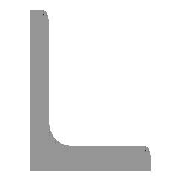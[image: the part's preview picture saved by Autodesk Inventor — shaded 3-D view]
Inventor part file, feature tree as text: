
AUTODESK INVENTOR PART (.ipt)
format: ipt  version: 2013 (Build 170138000, 138)  size: 116,736 bytes
history: native  units: mm (DEFAULTED — no unit token found)
features: other x4, sketch x2, plane x1
ambient origin geometry x8: Origin, YZ Plane, XZ Plane, XY Plane, X Axis, Y Axis, Z Axis, Center Point
bodies: Solid1 (feature_tree), Body (feature_tree)
feature tree (7):
  other  "GE-13015-01"
  other  "Driven Length"
  other  "Start plane"
  other  "End plane"
  sketch  "Sketch3"  dims[d0=76.2mm]
  plane  "Work Plane3"
  sketch  "Sketch4"  dims[d1=76.2mm d2=6.35mm d3=6.35mm d4=2184.4mm d5=0.0mm d10=0.0mm d11=0.0mm d12=-0.0mm d13=2184.4mm d14=7.874mm d15=3.81mm d16=90.0deg d17=2184.4mm]
